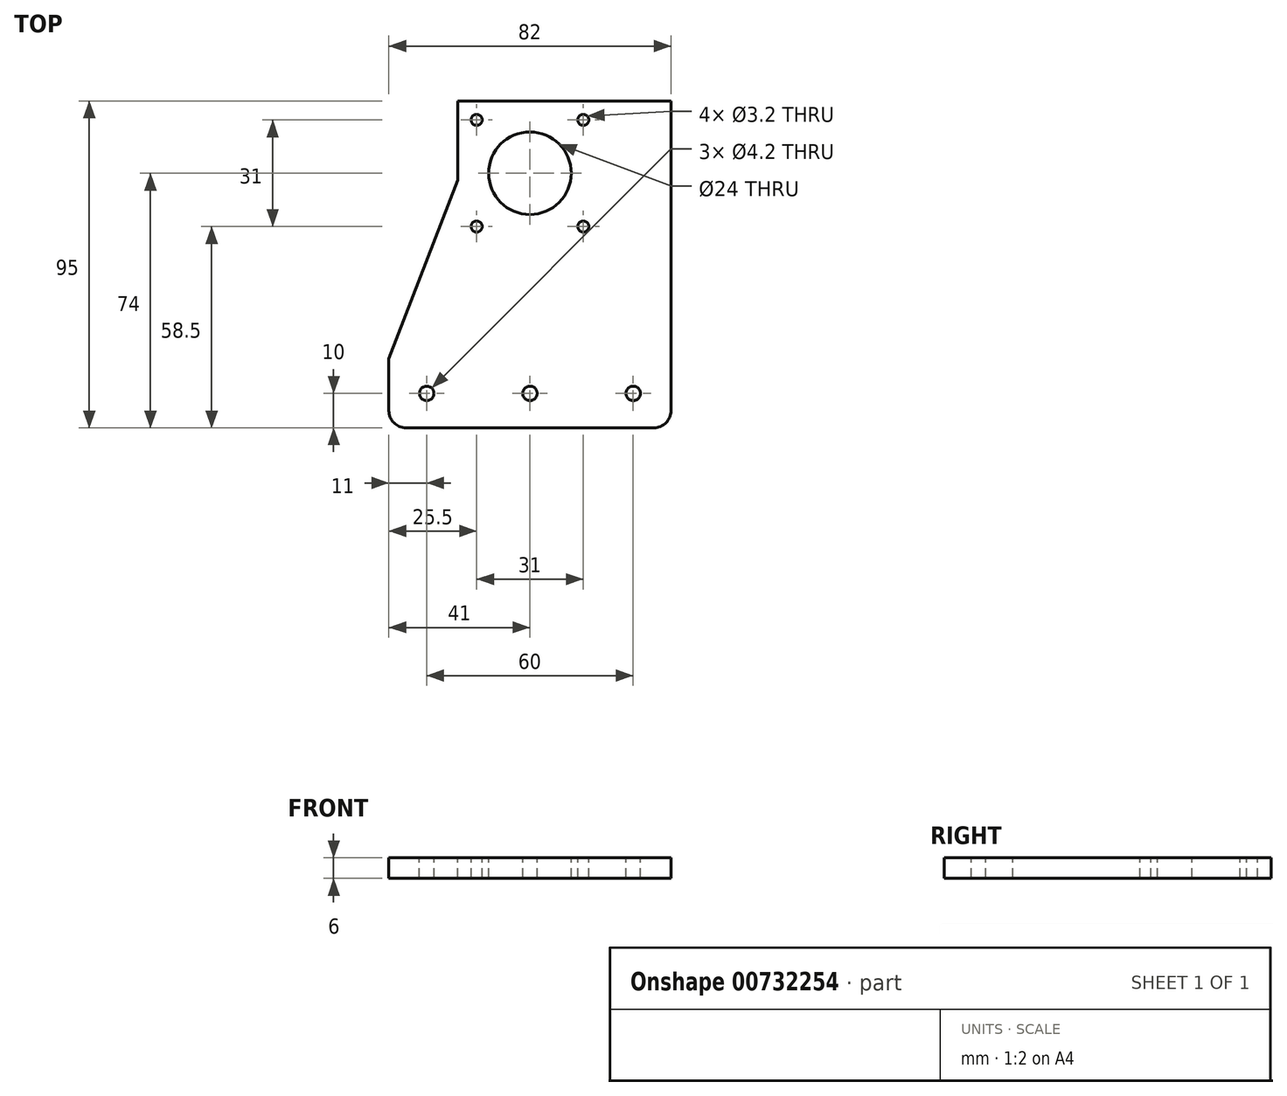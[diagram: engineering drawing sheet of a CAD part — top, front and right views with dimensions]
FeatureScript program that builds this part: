
annotation { "Feature Type Name" : "Feature", "Feature Type Description" : "" }
export const myFeature = defineFeature(function(context is Context, id is Id, definition is map)
    precondition{}
    {
        {
            var Q0;
            Q0=qCreatedBy(makeId("Top.planeOp"),FACE);
            var sketch = newSketch(context, id + "F0", { "sketchPlane" : qUnion([Q0])});
            skLineSegment(sketch, "E0.bottom", {"start": v(41, -47.5) * mm, "end": v(-41, -47.5) * mm});
            skLineSegment(sketch, "E0.top", {"start": v(41, 47.5) * mm, "end": v(-41, 47.5) * mm});
            skLineSegment(sketch, "E0.left", {"start": v(41, -47.5) * mm, "end": v(41, 47.5) * mm});
            skLineSegment(sketch, "E0.right", {"start": v(-41, -47.5) * mm, "end": v(-41, 47.5) * mm});
            skPoint(sketch, "E0.middle", {"position": v(0, 0) * mm});
            skSolve(sketch);
        }
        {
            var Q0;
            Q0=qSketchRegion(id+"F0",true);
            extrude(context, id + "F1", {"entities" : qUnion([Q0]), "depth" : 6 * mm, "offsetDistance" : 25 * mm});
        }
        {
            var Q0;
            Q0=makeQuery(id+"F1.opExtrude","CAP_FACE",FACE,{"disambiguationData":[OSD([sQuery(id+"F0.wireOp",EDGE,"E0.bottom"),sQuery(id+"F0.wireOp",EDGE,"E0.top"),sQuery(id+"F0.wireOp",EDGE,"E0.left"),sQuery(id+"F0.wireOp",EDGE,"E0.right")])],"isStart":false});
            var sketch = newSketch(context, id + "F2", { "sketchPlane" : qUnion([Q0])});
            skLineSegment(sketch, "E1", {"start": v(-21, 24.5) * mm, "end": v(-21, 47.5) * mm});
            skLineSegment(sketch, "E2", {"start": v(-21, 47.5) * mm, "end": v(-41, 47.5) * mm});
            skLineSegment(sketch, "E3", {"start": v(-41, 47.5) * mm, "end": v(-41, -27.5) * mm});
            skLineSegment(sketch, "E4", {"start": v(-41, -27.5) * mm, "end": v(-21, 24.5) * mm});
            skSolve(sketch);
        }
        {
            var Q0;
            Q0=qSketchRegion(id+"F2",true);
            extrude(context, id + "F3", {"entities" : qUnion([Q0]), "operationType" : NewBodyOperationType.REMOVE, "endBound" : BoundingType.THROUGH_ALL, "oppositeDirection" : true, "depth" : 25 * mm, "offsetDistance" : 25 * mm});
        }
        {
            var Q0;
            Q0=makeQuery(id+"F1.opExtrude","CAP_FACE",FACE,{"disambiguationData":[OSD([sQuery(id+"F0.wireOp",EDGE,"E0.bottom"),sQuery(id+"F0.wireOp",EDGE,"E0.top"),sQuery(id+"F0.wireOp",EDGE,"E0.left"),sQuery(id+"F0.wireOp",EDGE,"E0.right")])],"isStart":false});
            var sketch = newSketch(context, id + "F4", { "sketchPlane" : qUnion([Q0])});
            skCircle(sketch, "E5", {"center": v(0, 26.5) * mm, "radius": 12 * mm});
            skLineSegment(sketch, "E6.bottom", {"start": v(15.5, 11) * mm, "end": v(-15.5, 11) * mm, "construction": true});
            skLineSegment(sketch, "E6.top", {"start": v(15.5, 42) * mm, "end": v(-15.5, 42) * mm, "construction": true});
            skLineSegment(sketch, "E6.left", {"start": v(15.5, 11) * mm, "end": v(15.5, 42) * mm, "construction": true});
            skLineSegment(sketch, "E6.right", {"start": v(-15.5, 11) * mm, "end": v(-15.5, 42) * mm, "construction": true});
            skCircle(sketch, "E7", {"center": v(15.5, 42) * mm, "radius": 1.6 * mm});
            skCircle(sketch, "E8", {"center": v(-15.5, 42) * mm, "radius": 1.6 * mm});
            skCircle(sketch, "E9", {"center": v(15.5, 11) * mm, "radius": 1.6 * mm});
            skCircle(sketch, "E10", {"center": v(-15.5, 11) * mm, "radius": 1.6 * mm});
            skCircle(sketch, "E11", {"center": v(-30, -37.5) * mm, "radius": 2.1 * mm});
            skCircle(sketch, "E12", {"center": v(0, -37.5) * mm, "radius": 2.1 * mm});
            skCircle(sketch, "E13", {"center": v(30, -37.5) * mm, "radius": 2.1 * mm});
            skSolve(sketch);
        }
        {
            var Q0;
            Q0=qSketchRegion(id+"F4",true);
            extrude(context, id + "F5", {"entities" : qUnion([Q0]), "operationType" : NewBodyOperationType.REMOVE, "endBound" : BoundingType.THROUGH_ALL, "oppositeDirection" : true, "depth" : 25 * mm, "offsetDistance" : 25 * mm});
        }
        {
            var Q0;
            Q0=makeQuery(id+"F1.opExtrude","SWEPT_EDGE",EDGE,{"disambiguationData":[OSD([sQuery(id+"F0.wireOp",EDGE,"E0.bottom"),sQuery(id+"F0.wireOp",EDGE,"E0.right")])]});
            var Q1;
            Q1=makeQuery(id+"F1.opExtrude","SWEPT_EDGE",EDGE,{"disambiguationData":[OSD([sQuery(id+"F0.wireOp",EDGE,"E0.bottom"),sQuery(id+"F0.wireOp",EDGE,"E0.left")])]});
            var Q2;
            Q2=makeQuery(id+"F3.boolean.opBoolean","COPY",EDGE,{"derivedFrom":makeQuery(id+"F3.opExtrude","SWEPT_EDGE",EDGE,{"disambiguationData":[OSD([sQuery(id+"F0.wireOp",EDGE,"E0.top"),sQuery(id+"F2.wireOp",EDGE,"E1"),sQuery(id+"F2.wireOp",EDGE,"E2")])]})});
            var Q3;
            Q3=makeQuery(id+"FvpYxneDh0xRNV3_1.1.F3.boolean.opBoolean","COPY",EDGE,{"derivedFrom":makeQuery(id+"FvpYxneDh0xRNV3_1.1.F3.opExtrude","SWEPT_EDGE",EDGE,{"disambiguationData":[OSD([sQuery(id+"F0.wireOp",EDGE,"E0.top"),sQuery(id+"F2.wireOp",EDGE,"E1"),sQuery(id+"F2.wireOp",EDGE,"E2")])]})});
            fillet(context, id + "F6", {"entities" : qUnion([Q0, Q1, Q2, Q3]), "radius" : 5 * mm, "tangentPropagation" : true, "allowEdgeOverflow" : false});
        }
    });
